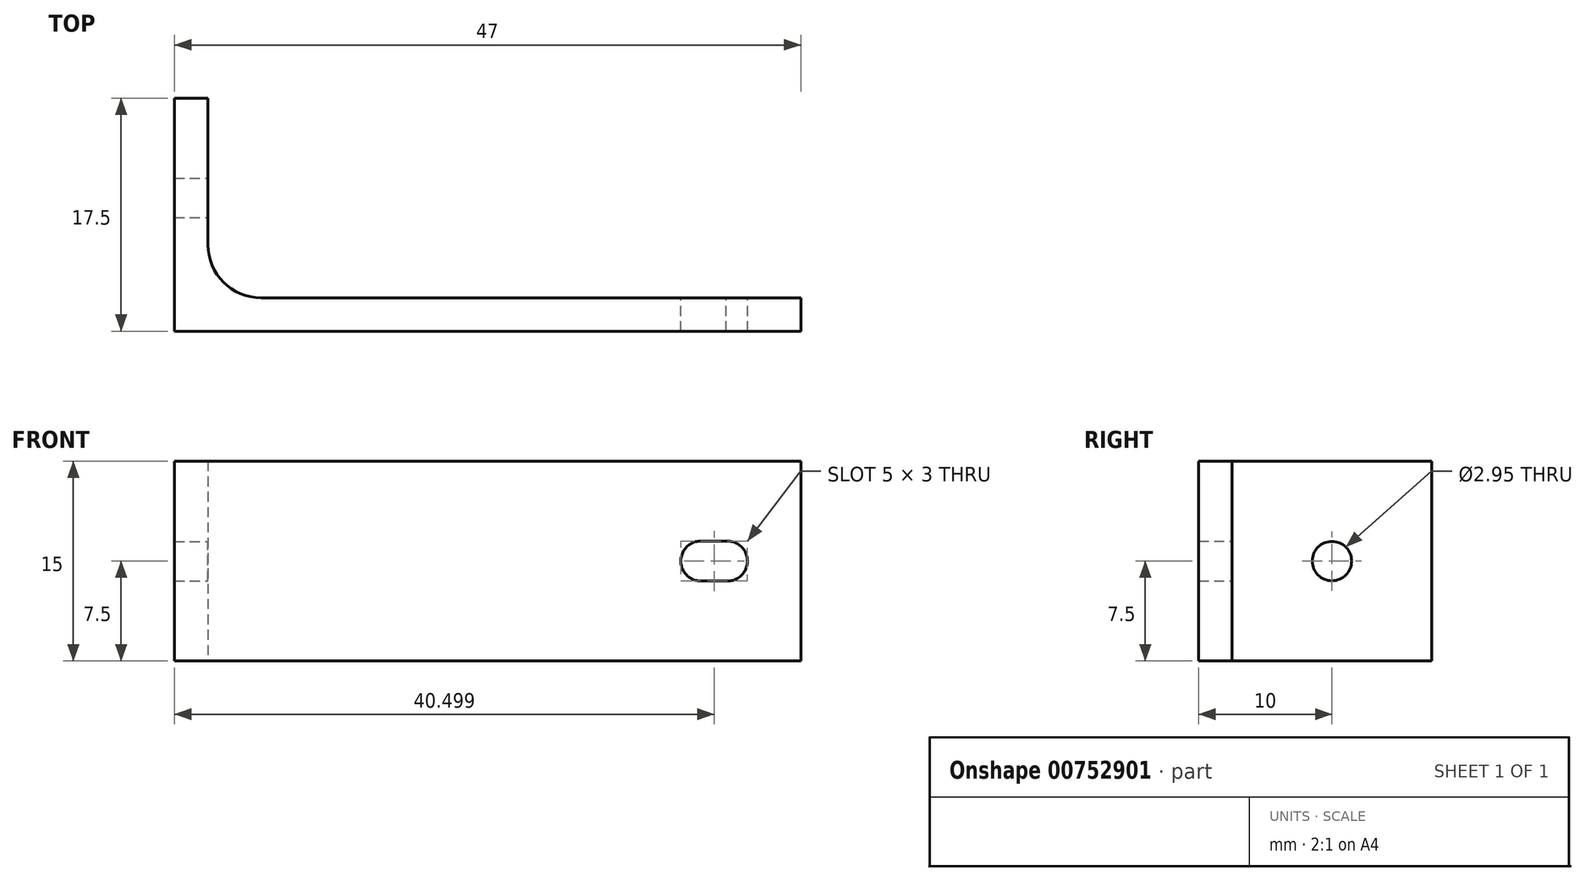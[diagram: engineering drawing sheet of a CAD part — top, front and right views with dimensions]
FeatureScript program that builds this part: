
annotation { "Feature Type Name" : "Feature", "Feature Type Description" : "" }
export const myFeature = defineFeature(function(context is Context, id is Id, definition is map)
    precondition{}
    {
        {
            var Q0;
            Q0=qCreatedBy(makeId("Top.planeOp"),FACE);
            var sketch = newSketch(context, id + "F0", { "sketchPlane" : qUnion([Q0])});
            skLineSegment(sketch, "E0", {"start": v(0, 0) * mm, "end": v(44.5, 0) * mm});
            skLineSegment(sketch, "E1", {"start": v(0, 15) * mm, "end": v(0, 0) * mm});
            skLineSegment(sketch, "E2", {"start": v(0, 15) * mm, "end": v(-2.5, 15) * mm});
            skLineSegment(sketch, "E3", {"start": v(-2.5, 15) * mm, "end": v(-2.5, -2.5) * mm});
            skLineSegment(sketch, "E4", {"start": v(-2.5, -2.5) * mm, "end": v(44.5, -2.5) * mm});
            skLineSegment(sketch, "E5", {"start": v(44.5, -2.5) * mm, "end": v(44.5, 0) * mm});
            skSolve(sketch);
        }
        {
            var Q0;
            Q0=qSketchRegion(id+"F0",true);
            extrude(context, id + "F1", {"entities" : qUnion([Q0]), "depth" : 15 * mm, "offsetDistance" : 25 * mm});
        }
        {
            var Q0;
            Q0=makeQuery(id+"F1.opExtrude","SWEPT_FACE",FACE,{"disambiguationData":[OSD([sQuery(id+"F0.wireOp",EDGE,"E1")])]});
            var sketch = newSketch(context, id + "F2", { "sketchPlane" : qUnion([Q0])});
            skLineSegment(sketch, "E6.0", {"start": v(15, 15) * mm, "end": v(15, 0) * mm, "construction": true});
            skLineSegment(sketch, "E6.1", {"start": v(0, 15) * mm, "end": v(0, 0) * mm, "construction": true});
            skLineSegment(sketch, "E6.2", {"start": v(15, 0) * mm, "end": v(0, 0) * mm, "construction": true});
            skLineSegment(sketch, "E6.3", {"start": v(15, 15) * mm, "end": v(0, 15) * mm, "construction": true});
            skLineSegment(sketch, "E7", {"start": v(15, 0) * mm, "end": v(0, 15) * mm, "construction": true});
            skCircle(sketch, "E8", {"center": v(7.5, 7.5) * mm, "radius": 1.48 * mm});
            skSolve(sketch);
        }
        {
            var Q0;
            Q0=sQuery(id+"F2.wireOp",VERTEX,"E8.center");
            var Q1;
            Q1=makeQuery(id+"F1.opExtrude","SWEPT_BODY",BODY,{"disambiguationData":[OSD([sQuery(id+"F0.wireOp",EDGE,"E0"),sQuery(id+"F0.wireOp",EDGE,"E1"),sQuery(id+"F0.wireOp",EDGE,"R3w78IRR-Ahmf-OLtC-FCrt-IJWMmAD78zOF"),sQuery(id+"F0.wireOp",EDGE,"E2"),sQuery(id+"F0.wireOp",EDGE,"E3"),sQuery(id+"F0.wireOp",EDGE,"N9y71L1L-vMLF-l9xB-yKLB-RcM4H2JnEg4h"),sQuery(id+"F0.wireOp",EDGE,"tQ4BxOPJ-s92R-gXy5-vMEL-6yIXJQTIRToP"),sQuery(id+"F0.wireOp",EDGE,"W29mj6k8-BBJY-nj1Z-NcPe-27QwrTbMPeB3"),sQuery(id+"F0.wireOp",EDGE,"U4CHrdOU-qw6W-kspJ-EBLW-1nSkqqJEMxHj"),sQuery(id+"F0.wireOp",EDGE,"SkZS9tSL-uJuA-Vk2N-TDRF-tH0H7Vp3IELU")])]});
            hole(context, id + "F3", {"style" : HoleStyle.SIMPLE, "endStyle" : HoleEndStyle.THROUGH, "holeDiameter" : 2.95 * mm, "majorDiameter" : 5 * mm, "isTappedThrough" : true, "tappedDepth" : 12 * mm, "tapClearance" : 3, "locations" : qUnion([Q0]), "scope" : qUnion([Q1])});
        }
        {
            var Q0;
            Q0=makeQuery(id+"F1.opExtrude","SWEPT_EDGE",EDGE,{"disambiguationData":[OSD([sQuery(id+"F0.wireOp",EDGE,"E0"),sQuery(id+"F0.wireOp",EDGE,"E1")])]});
            fillet(context, id + "F4", {"entities" : qUnion([Q0]), "radius" : 4 * mm, "tangentPropagation" : true, "allowEdgeOverflow" : false});
        }
        {
            var Q0;
            Q0=makeQuery(id+"F1.opExtrude","SWEPT_FACE",FACE,{"disambiguationData":[OSD([sQuery(id+"F0.wireOp",EDGE,"E0")])]});
            var sketch = newSketch(context, id + "F5", { "sketchPlane" : qUnion([Q0])});
            skLineSegment(sketch, "E9.0", {"start": v(-4, 15) * mm, "end": v(-44.5, 15) * mm, "construction": true});
            skLineSegment(sketch, "E9.1", {"start": v(-4, 0) * mm, "end": v(-44.5, 0) * mm, "construction": true});
            skLineSegment(sketch, "E9.2", {"start": v(-4, 0) * mm, "end": v(-4, 15) * mm, "construction": true});
            skLineSegment(sketch, "E9.3", {"start": v(-44.5, 15) * mm, "end": v(-44.5, 0) * mm, "construction": true});
            skLineSegment(sketch, "E10", {"start": v(-4, 7.5) * mm, "end": v(-37, 7.5) * mm, "construction": true});
            skArc(sketch, "E11", {"start": v(-37, 6) * mm, "mid": v(-35.5, 7.5) * mm, "end": v(-37, 9) * mm});
            skLineSegment(sketch, "E12", {"start": v(-37, 7.5) * mm, "end": v(-39, 7.5) * mm, "construction": true});
            skArc(sketch, "E13", {"start": v(-38.89, 9) * mm, "mid": v(-40.5, 7.56) * mm, "end": v(-39, 6) * mm});
            skLineSegment(sketch, "E14", {"start": v(-39, 6) * mm, "end": v(-37, 6) * mm});
            skLineSegment(sketch, "E15", {"start": v(-38.89, 9) * mm, "end": v(-37, 9) * mm});
            skSolve(sketch);
        }
        {
            var Q0;
            Q0=makeQuery(id+"F5.imprint","IMPRINT",FACE,{"disambiguationData":[TD([[makeQuery(id+"F5.imprint","IMPRINT",EDGE,{"derivedFrom":sQuery(id+"F5.wireOp",EDGE,"E11")}),1.0]])]});
            extrude(context, id + "F6", {"entities" : qUnion([Q0]), "operationType" : NewBodyOperationType.REMOVE, "oppositeDirection" : true, "depth" : 25 * mm, "offsetDistance" : 25 * mm});
        }
    });
